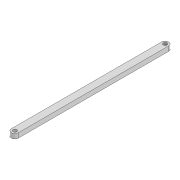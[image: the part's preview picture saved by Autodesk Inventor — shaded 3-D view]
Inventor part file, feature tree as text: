
AUTODESK INVENTOR PART (.ipt)
format: ipt  version: 2022 (Build 260153000, 153)  size: 89,088 bytes
history: native  units: mm
features: extrude x1, sketch x1
ambient origin geometry x8: Origin, YZ Plane, XZ Plane, XY Plane, X Axis, Y Axis, Z Axis, Center Point
bodies: Solid1 (feature_tree)
feature tree (2):
  extrude  "Extrusion1"  Depth=4.0mm
  sketch  "Sketch1"  dims[d0=3.2mm d1=3.2mm d2=6.0mm d3=128.523mm d6=4.0mm d7=0.0mm]
